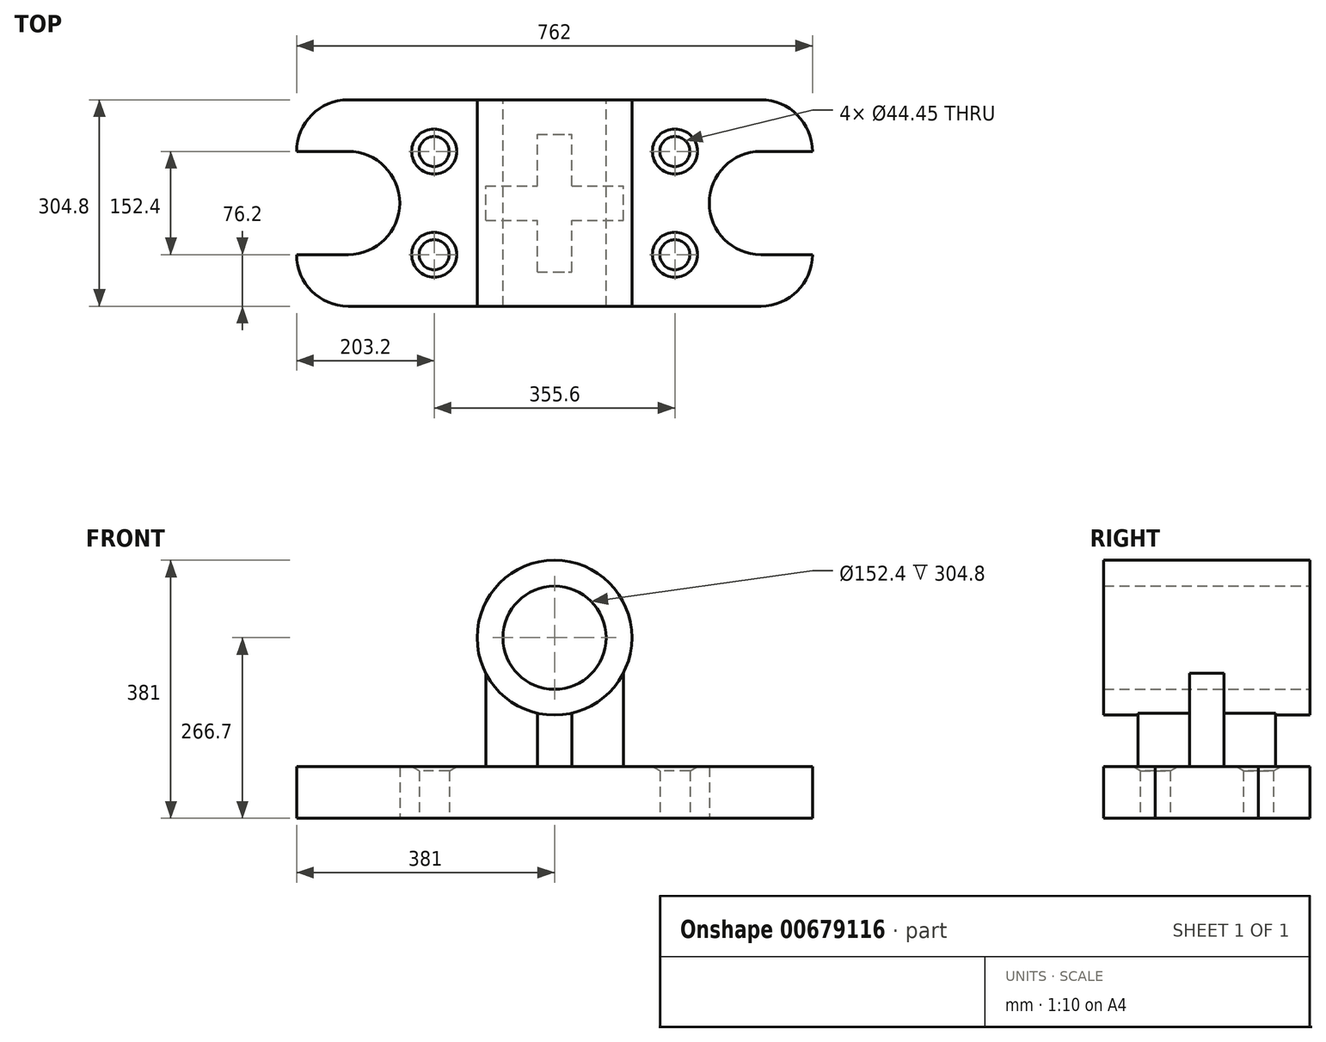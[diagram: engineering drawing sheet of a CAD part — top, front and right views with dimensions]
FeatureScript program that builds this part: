
annotation { "Feature Type Name" : "Feature", "Feature Type Description" : "" }
export const myFeature = defineFeature(function(context is Context, id is Id, definition is map)
    precondition{}
    {
        {
            var Q0;
            Q0=qCreatedBy(makeId("Top.planeOp"),FACE);
            var sketch = newSketch(context, id + "F0", { "sketchPlane" : qUnion([Q0])});
            skLineSegment(sketch, "E0.bottom", {"start": v(-304.8, 152.4) * mm, "end": v(304.8, 152.4) * mm});
            skLineSegment(sketch, "E0.top", {"start": v(-304.8, -152.4) * mm, "end": v(304.8, -152.4) * mm});
            skPoint(sketch, "E0.middle", {"position": v(0, 0) * mm});
            skLineSegment(sketch, "E1.0", {"start": v(-381, 76.2) * mm, "end": v(-304.8, 76.2) * mm});
            skLineSegment(sketch, "E2.0", {"start": v(-381, -76.2) * mm, "end": v(-304.8, -76.2) * mm});
            skPoint(sketch, "E3.visualSharp", {"position": v(-381, 152.4) * mm});
            skArc(sketch, "E3.filletArc", {"start": v(-304.8, 152.4) * mm, "mid": v(-358.68, 130.08) * mm, "end": v(-381, 76.2) * mm});
            skPoint(sketch, "E4.visualSharp", {"position": v(-381, -152.4) * mm});
            skArc(sketch, "E4.filletArc", {"start": v(-381, -76.2) * mm, "mid": v(-358.68, -130.08) * mm, "end": v(-304.8, -152.4) * mm});
            skPoint(sketch, "E5.visualSharp", {"position": v(381, 152.4) * mm});
            skArc(sketch, "E5.filletArc", {"start": v(381, 76.2) * mm, "mid": v(358.68, 130.08) * mm, "end": v(304.8, 152.4) * mm});
            skPoint(sketch, "E6.visualSharp", {"position": v(381, -152.4) * mm});
            skArc(sketch, "E6.filletArc", {"start": v(304.8, -152.4) * mm, "mid": v(358.68, -130.08) * mm, "end": v(381, -76.2) * mm});
            skLineSegment(sketch, "E7.trimOffspring", {"start": v(304.8, 76.2) * mm, "end": v(381, 76.2) * mm});
            skLineSegment(sketch, "E8.trimOffspring", {"start": v(304.8, -76.2) * mm, "end": v(381, -76.2) * mm});
            skArc(sketch, "E9", {"start": v(304.8, 76.2) * mm, "mid": v(228.6, 0) * mm, "end": v(304.8, -76.2) * mm});
            skArc(sketch, "E10", {"start": v(-304.8, -76.2) * mm, "mid": v(-228.6, 0) * mm, "end": v(-304.8, 76.2) * mm});
            skCircle(sketch, "E11", {"center": v(-177.8, 76.2) * mm, "radius": 22.23 * mm});
            skCircle(sketch, "E12", {"center": v(-177.8, 76.2) * mm, "radius": 38.1 * mm});
            skCircle(sketch, "E13", {"center": v(-177.8, -76.2) * mm, "radius": 22.23 * mm});
            skCircle(sketch, "E14", {"center": v(-177.8, -76.2) * mm, "radius": 38.1 * mm});
            skCircle(sketch, "E15", {"center": v(177.8, -76.2) * mm, "radius": 22.23 * mm});
            skCircle(sketch, "E16", {"center": v(177.8, -76.2) * mm, "radius": 38.1 * mm});
            skCircle(sketch, "E17", {"center": v(177.8, 76.2) * mm, "radius": 22.23 * mm});
            skCircle(sketch, "E18", {"center": v(177.8, 76.2) * mm, "radius": 38.1 * mm});
            skLineSegment(sketch, "E19", {"start": v(-114.3, 152.4) * mm, "end": v(-114.3, -152.4) * mm});
            skLineSegment(sketch, "E20", {"start": v(114.3, 152.4) * mm, "end": v(114.3, -152.4) * mm});
            skSolve(sketch);
        }
        {
            var Q0;
            Q0=makeQuery(id+"F0.imprint","IMPRINT",FACE,{"disambiguationData":[TD([[makeQuery(id+"F0.imprint","IMPRINT",EDGE,{"derivedFrom":sQuery(id+"F0.wireOp",EDGE,"E1.0")}),1.0]])]});
            var Q1;
            {var subQ0=sQuery(id+"F0.wireOp",EDGE,"E19");Q1=makeQuery(id+"F0.imprint","IMPRINT",FACE,{"disambiguationData":[TD([[makeQuery(id+"F0.imprint","IMPRINT",EDGE,{"derivedFrom":subQ0}),1.0]])]});}
            var Q2;
            {var subQ1=sQuery(id+"F0.wireOp",EDGE,"E5.filletArc");Q2=makeQuery(id+"F0.imprint","IMPRINT",FACE,{"disambiguationData":[TD([[makeQuery(id+"F0.imprint","IMPRINT",EDGE,{"derivedFrom":subQ1}),1.0]])]});}
            var Q3;
            Q3=makeQuery(id+"F0.imprint","IMPRINT",FACE,{"disambiguationData":[TD([[makeQuery(id+"F0.imprint","IMPRINT",EDGE,{"derivedFrom":sQuery(id+"F0.wireOp",EDGE,"E17")}),-1.0]])]});
            var Q4;
            Q4=makeQuery(id+"F0.imprint","IMPRINT",FACE,{"disambiguationData":[TD([[makeQuery(id+"F0.imprint","IMPRINT",EDGE,{"derivedFrom":sQuery(id+"F0.wireOp",EDGE,"E15")}),-1.0]])]});
            var Q5;
            Q5=makeQuery(id+"F0.imprint","IMPRINT",FACE,{"disambiguationData":[TD([[makeQuery(id+"F0.imprint","IMPRINT",EDGE,{"derivedFrom":sQuery(id+"F0.wireOp",EDGE,"E13")}),-1.0]])]});
            var Q6;
            Q6=makeQuery(id+"F0.imprint","IMPRINT",FACE,{"disambiguationData":[TD([[makeQuery(id+"F0.imprint","IMPRINT",EDGE,{"derivedFrom":sQuery(id+"F0.wireOp",EDGE,"E11")}),-1.0]])]});
            extrude(context, id + "F1", {"entities" : qUnion([Q0, Q1, Q2, Q3, Q4, Q5, Q6]), "depth" : 76.2 * mm, "offsetDistance" : 25.4 * mm});
        }
        {
            var Q0;
            Q0=makeQuery(id+"F1.opExtrude","CAP_EDGE",EDGE,{"disambiguationData":[OSD([sQuery(id+"F0.wireOp",EDGE,"E11")])],"isStart":false});
            var Q1;
            Q1=makeQuery(id+"F1.opExtrude","CAP_EDGE",EDGE,{"disambiguationData":[OSD([sQuery(id+"F0.wireOp",EDGE,"E13")])],"isStart":false});
            var Q2;
            Q2=makeQuery(id+"F1.opExtrude","CAP_EDGE",EDGE,{"disambiguationData":[OSD([sQuery(id+"F0.wireOp",EDGE,"E15")])],"isStart":false});
            var Q3;
            Q3=makeQuery(id+"F1.opExtrude","CAP_EDGE",EDGE,{"disambiguationData":[OSD([sQuery(id+"F0.wireOp",EDGE,"E17")])],"isStart":false});
            chamfer(context, id + "F2", {"entities" : qUnion([Q0, Q1, Q2, Q3]), "chamferType" : ChamferType.OFFSET_ANGLE, "width" : 6.35 * mm, "oppositeDirection" : false, "angle" : 60 * degree, "tangentPropagation" : true});
        }
        {
            var Q0;
            Q0=qCreatedBy(makeId("Front.planeOp"),FACE);
            var sketch = newSketch(context, id + "F3", { "sketchPlane" : qUnion([Q0])});
            skCircle(sketch, "E21", {"center": v(0, 266.7) * mm, "radius": 114.3 * mm});
            skCircle(sketch, "E22", {"center": v(0, 266.7) * mm, "radius": 76.2 * mm});
            skLineSegment(sketch, "E23", {"start": v(101.6, 214.34) * mm, "end": v(101.6, 76.2) * mm});
            skLineSegment(sketch, "E24", {"start": v(-101.6, 214.34) * mm, "end": v(-101.6, 76.2) * mm});
            skLineSegment(sketch, "E25", {"start": v(-25.4, 155.26) * mm, "end": v(-25.4, 76.2) * mm});
            skLineSegment(sketch, "E26", {"start": v(25.4, 155.26) * mm, "end": v(25.4, 76.2) * mm});
            skLineSegment(sketch, "E27", {"start": v(-101.6, 76.2) * mm, "end": v(-25.4, 76.2) * mm});
            skLineSegment(sketch, "E28", {"start": v(25.4, 76.2) * mm, "end": v(101.6, 76.2) * mm});
            skLineSegment(sketch, "E29", {"start": v(-25.4, 76.2) * mm, "end": v(25.4, 76.2) * mm});
            skSolve(sketch);
        }
        {
            var Q0;
            {var subQ0=sQuery(id+"F3.wireOp",EDGE,"E25");Q0=makeQuery(id+"F3.imprint","IMPRINT",FACE,{"disambiguationData":[TD([[makeQuery(id+"F3.imprint","IMPRINT",EDGE,{"derivedFrom":subQ0}),1.0]])]});}
            extrude(context, id + "F4", {"entities" : qUnion([Q0]), "operationType" : NewBodyOperationType.ADD, "endBound" : BoundingType.SYMMETRIC, "depth" : 203.2 * mm, "offsetDistance" : 25.4 * mm});
        }
        {
            var Q0;
            {var subQ0=sQuery(id+"F3.wireOp",EDGE,"E23");Q0=makeQuery(id+"F3.imprint","IMPRINT",FACE,{"disambiguationData":[TD([[makeQuery(id+"F3.imprint","IMPRINT",EDGE,{"derivedFrom":subQ0}),-1.0]])]});}
            var Q1;
            {var subQ0=sQuery(id+"F3.wireOp",EDGE,"E24");Q1=makeQuery(id+"F3.imprint","IMPRINT",FACE,{"disambiguationData":[TD([[makeQuery(id+"F3.imprint","IMPRINT",EDGE,{"derivedFrom":subQ0}),1.0]])]});}
            extrude(context, id + "F5", {"entities" : qUnion([Q0, Q1]), "operationType" : NewBodyOperationType.ADD, "endBound" : BoundingType.SYMMETRIC, "depth" : 50.8 * mm, "offsetDistance" : 25.4 * mm});
        }
        {
            var Q0;
            Q0=makeQuery(id+"F3.imprint","IMPRINT",FACE,{"disambiguationData":[TD([[makeQuery(id+"F3.imprint","IMPRINT",EDGE,{"derivedFrom":sQuery(id+"F3.wireOp",EDGE,"E22")}),-1.0]])]});
            extrude(context, id + "F6", {"entities" : qUnion([Q0]), "operationType" : NewBodyOperationType.ADD, "endBound" : BoundingType.SYMMETRIC, "depth" : 304.8 * mm, "offsetDistance" : 25.4 * mm});
        }
    });
